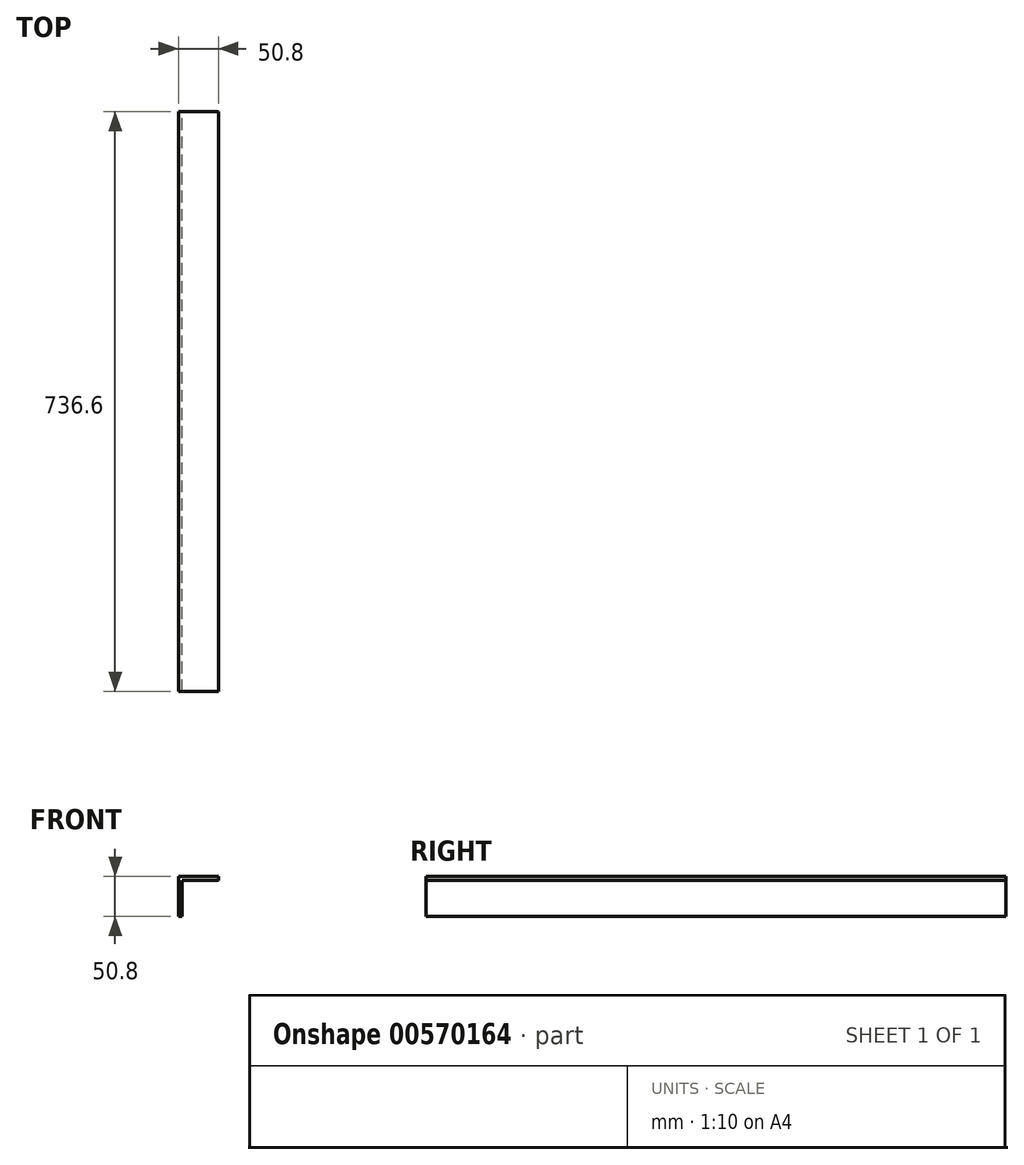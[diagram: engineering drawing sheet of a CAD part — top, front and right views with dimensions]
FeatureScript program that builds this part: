
annotation { "Feature Type Name" : "Feature", "Feature Type Description" : "" }
export const myFeature = defineFeature(function(context is Context, id is Id, definition is map)
    precondition{}
    {
        {
            var Q0;
            Q0=qCreatedBy(makeId("Front.planeOp"),FACE);
            var sketch = newSketch(context, id + "F0", { "sketchPlane" : qUnion([Q0])});
            skLineSegment(sketch, "E0", {"start": v(0, 50.8) * mm, "end": v(0, 0) * mm});
            skLineSegment(sketch, "E1", {"start": v(0, 0) * mm, "end": v(4.76, 0) * mm});
            skLineSegment(sketch, "E2", {"start": v(4.76, 0) * mm, "end": v(4.76, 46.04) * mm});
            skLineSegment(sketch, "E3", {"start": v(4.76, 46.04) * mm, "end": v(50.8, 46.04) * mm});
            skLineSegment(sketch, "E4", {"start": v(0, 50.8) * mm, "end": v(50.8, 50.8) * mm});
            skLineSegment(sketch, "E5", {"start": v(50.8, 50.8) * mm, "end": v(50.8, 46.04) * mm});
            skSolve(sketch);
        }
        {
            var Q0;
            Q0=makeQuery(id+"F0.imprint","IMPRINT",FACE,{"disambiguationData":[TD([[makeQuery(id+"F0.imprint","IMPRINT",EDGE,{"derivedFrom":sQuery(id+"F0.wireOp",EDGE,"E0")}),1.0]])]});
            extrude(context, id + "F1", {"entities" : qUnion([Q0]), "depth" : 736.6 * mm, "offsetDistance" : 25.4 * mm});
        }
    });
